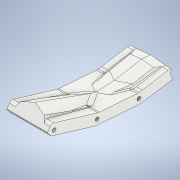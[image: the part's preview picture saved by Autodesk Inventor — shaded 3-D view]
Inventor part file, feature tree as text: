
AUTODESK INVENTOR PART (.ipt)
format: ipt  version: 2020.4 (Build 244396010, 396A)  size: 298,496 bytes
history: native  units: in
note: dims shown in document units (in); Inventor stores cm internally (conversion verified against a paired STEP export)
features: extrude x3, sketch x3, projected_geometry x2
ambient origin geometry x8: Origin, YZ Plane, XZ Plane, XY Plane, X Axis, Y Axis, Z Axis, Center Point
bodies: Solid2 (feature_tree), Solid1 (feature_tree)
feature tree (8):
  extrude  "Extrusion1"  Depth=0.126in
  extrude  "Extrusion2"  Depth=0.3937in TaperAngle=0.0deg
  extrude  "Extrusion3"  Depth=0.1969in TaperAngle=0.0deg
  sketch  "Sketch1"  dims[d0=0.126in d1=0.126in]
  sketch  "Sketch2"  dims[d2=0.126in d3=0.3937in d4=0.0in]
  projected_geometry  "Projected Loop1"
  sketch  "Sketch3"  dims[d5=0.1969in d6=0.0in d7=0.1969in d8=0.0in]
  projected_geometry  "Projected Loop2"
